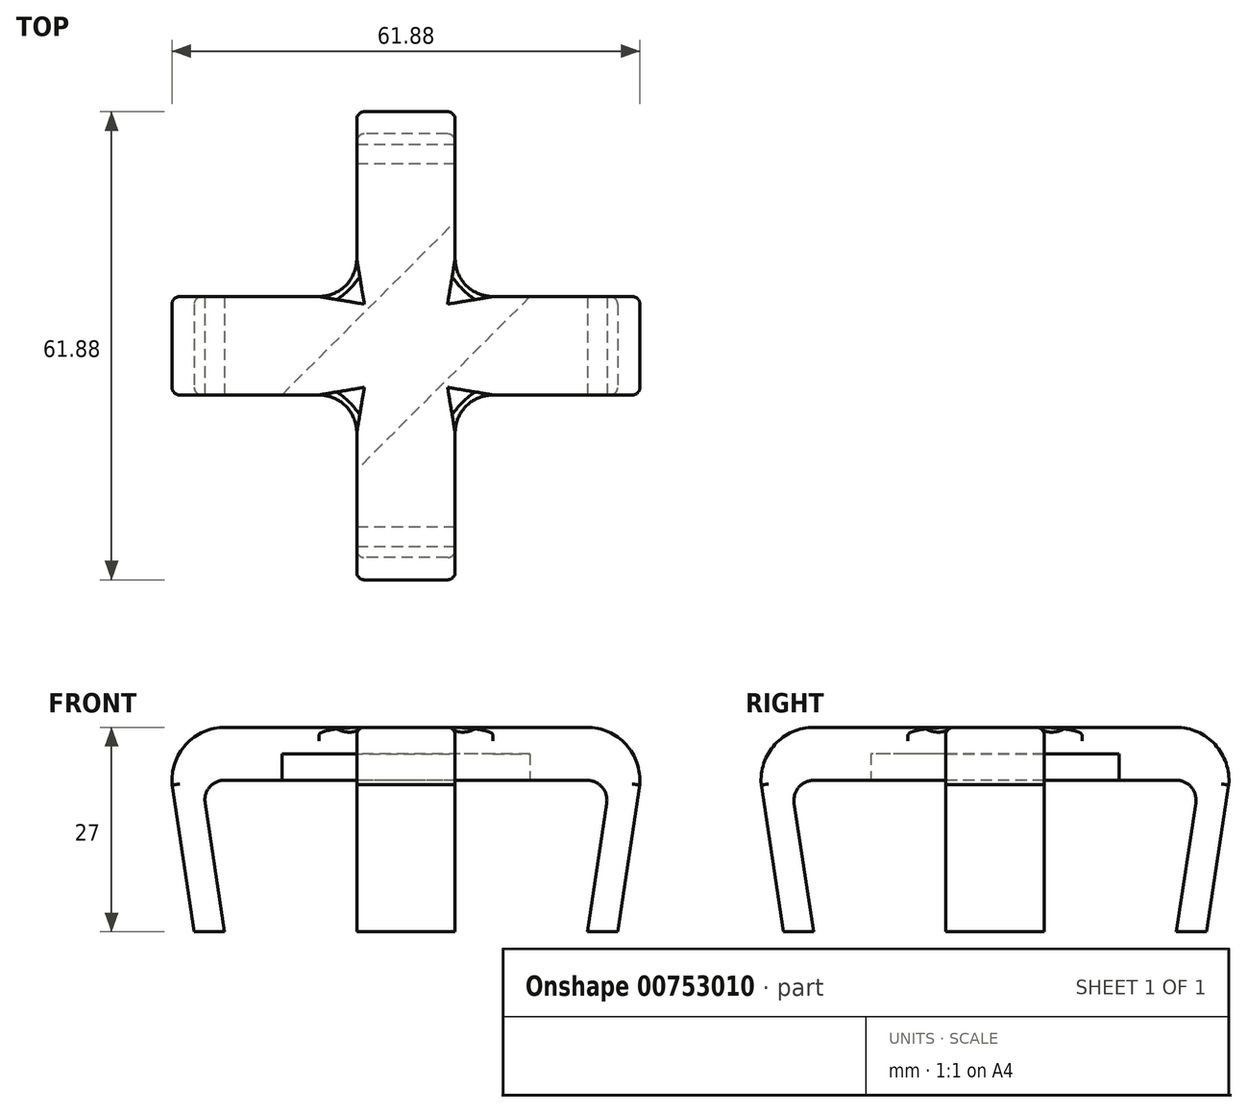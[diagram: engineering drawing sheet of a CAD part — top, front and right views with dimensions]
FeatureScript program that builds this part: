
annotation { "Feature Type Name" : "Feature", "Feature Type Description" : "" }
export const myFeature = defineFeature(function(context is Context, id is Id, definition is map)
    precondition{}
    {
        {
            var Q0;
            Q0=qCreatedBy(makeId("Top.planeOp"),FACE);
            var sketch = newSketch(context, id + "F0", { "sketchPlane" : qUnion([Q0])});
            skLineSegment(sketch, "E0", {"start": v(0, 0) * mm, "end": v(24, 0) * mm});
            skLineSegment(sketch, "E1", {"start": v(0, 0) * mm, "end": v(-24, 0) * mm});
            skLineSegment(sketch, "E2", {"start": v(-24, 20) * mm, "end": v(-28, 20) * mm});
            skLineSegment(sketch, "E3", {"start": v(28, 20) * mm, "end": v(24, 20) * mm});
            skLineSegment(sketch, "E4", {"start": v(-24, 20) * mm, "end": v(-24, 0) * mm, "construction": true});
            skLineSegment(sketch, "E5", {"start": v(-24, 0) * mm, "end": v(-27, 0) * mm, "construction": true});
            skLineSegment(sketch, "E6", {"start": v(24, 0) * mm, "end": v(27, 0) * mm, "construction": true});
            skLineSegment(sketch, "E7", {"start": v(28, 20) * mm, "end": v(30.91, 0.59) * mm});
            skLineSegment(sketch, "E8", {"start": v(30.91, 0.59) * mm, "end": v(27, 0) * mm, "construction": true});
            skLineSegment(sketch, "E9", {"start": v(-28, 20) * mm, "end": v(-30.91, 0.59) * mm});
            skLineSegment(sketch, "E10", {"start": v(-30.91, 0.59) * mm, "end": v(-27, 0) * mm, "construction": true});
            skLineSegment(sketch, "E11", {"start": v(0, 0) * mm, "end": v(0, -7) * mm, "construction": true});
            skLineSegment(sketch, "E12", {"start": v(23.94, -7) * mm, "end": v(-23.94, -7) * mm});
            skArc(sketch, "E13", {"start": v(23.94, -7) * mm, "mid": v(29.09, -4.74) * mm, "end": v(30.91, 0.59) * mm});
            skArc(sketch, "E14", {"start": v(-23.94, -7) * mm, "mid": v(-29.09, -4.74) * mm, "end": v(-30.91, 0.59) * mm});
            skArc(sketch, "E15", {"start": v(-24, 0) * mm, "mid": v(-25.96, 0.9) * mm, "end": v(-26.55, 2.97) * mm});
            skLineSegment(sketch, "E16", {"start": v(24, 20) * mm, "end": v(23.94, 0) * mm, "construction": true});
            skArc(sketch, "E17", {"start": v(24, 0) * mm, "mid": v(25.96, 0.93) * mm, "end": v(26.55, 3.02) * mm});
            skLineSegment(sketch, "E18", {"start": v(24, 20) * mm, "end": v(26.55, 3.02) * mm});
            skLineSegment(sketch, "E19", {"start": v(26.55, 3.02) * mm, "end": v(27, 0) * mm, "construction": true});
            skLineSegment(sketch, "E20", {"start": v(-24, 20) * mm, "end": v(-26.55, 2.97) * mm});
            skLineSegment(sketch, "E21", {"start": v(-26.55, 2.97) * mm, "end": v(-27, 0) * mm, "construction": true});
            skSolve(sketch);
        }
        {
            var Q0;
            Q0=makeQuery(id+"F0.imprint","IMPRINT",FACE,{"disambiguationData":[TD([[makeQuery(id+"F0.imprint","IMPRINT",EDGE,{"derivedFrom":sQuery(id+"F0.wireOp",EDGE,"E0")}),-1.0]])]});
            extrude(context, id + "F1", {"entities" : qUnion([Q0]), "depth" : 13 * mm, "offsetDistance" : 25 * mm});
        }
        {
            var Q0;
            Q0=makeQuery(id+"F1.opExtrude","SWEPT_BODY",BODY,{"disambiguationData":[OSD([sQuery(id+"F0.wireOp",EDGE,"E0"),sQuery(id+"F0.wireOp",EDGE,"E1"),sQuery(id+"F0.wireOp",EDGE,"GqOIY193-nnTG-WNAK-7P5C-qbdsJhsmqnTg"),sQuery(id+"F0.wireOp",EDGE,"nFv10fVA-e4Zq-mQEx-yQo5-pWFaT3uSzO8I"),sQuery(id+"F0.wireOp",EDGE,"E2"),sQuery(id+"F0.wireOp",EDGE,"2eDGChY6-uomO-ZvTw-BVGf-heDjoFAaIxCZ"),sQuery(id+"F0.wireOp",EDGE,"AwENzGN6-6Jdi-Xnei-QJyw-jy8g0ptfrepB"),sQuery(id+"F0.wireOp",EDGE,"pxZ1h7P2-Ql5e-nRXq-oBCs-k8CSoZiUGTe5"),sQuery(id+"F0.wireOp",EDGE,"jQoMa6uT-SFcK-1EqK-lPNF-uQxbUQPNmj6G"),sQuery(id+"F0.wireOp",EDGE,"E3"),sQuery(id+"F0.wireOp",EDGE,"ouRIi9zz-WExV-jkmE-XCtQ-bmmSq9bP91mH"),sQuery(id+"F0.wireOp",EDGE,"O0WKsKBU-VN61-qjR9-eNNd-4MIzQNMGMWZd"),sQuery(id+"F0.wireOp",EDGE,"a8fOSSVA-k9Fx-iGqo-vGb5-aITEA6sK3hfp")])]});
            var Q1;
            {var subQ0=sQuery(id+"F0.wireOp",EDGE,"nFv10fVA-e4Zq-mQEx-yQo5-pWFaT3uSzO8I");var subQ1=sQuery(id+"F0.wireOp",EDGE,"GqOIY193-nnTG-WNAK-7P5C-qbdsJhsmqnTg");var subQ2=sQuery(id+"F0.wireOp",EDGE,"O0WKsKBU-VN61-qjR9-eNNd-4MIzQNMGMWZd");var subQ3=sQuery(id+"F0.wireOp",EDGE,"E1");var subQ4=sQuery(id+"F0.wireOp",EDGE,"E0");Q1=makeQuery(id+"F5.boolean.opBoolean","SPLIT",EDGE,{"disambiguationData":[TD([makeQuery(id+"F4.opFillet","BLEND_FACE",FACE,{"disambiguationData":[OSD([subQ1,subQ0])]})])],"derivedFrom":makeQuery(id+"F1.opExtrude","CAP_EDGE",EDGE,{"disambiguationData":[OSD([subQ4,subQ3,subQ1,subQ2])],"isStart":true})});}
            transform(context, id + "F2", {"entities" : qUnion([Q0]), "transformType" : TransformType.ROTATION, "transformAxis" : qUnion([Q1]), "angle" : 90 * degree, "oppositeDirection" : true, "makeCopy" : false});
        }
        {
            var Q0;
            Q0=qCreatedBy(makeId("Right.planeOp"),FACE);
            var sketch = newSketch(context, id + "F3", { "sketchPlane" : qUnion([Q0])});
            skLineSegment(sketch, "E22.bottom", {"start": v(13, 0) * mm, "end": v(0, 0) * mm, "construction": true});
            skLineSegment(sketch, "E22.top", {"start": v(13, 7) * mm, "end": v(0, 7) * mm, "construction": true});
            skLineSegment(sketch, "E22.left", {"start": v(0, 7) * mm, "end": v(0, 0) * mm, "construction": true});
            skLineSegment(sketch, "E22.right", {"start": v(13, 7) * mm, "end": v(13, 0) * mm, "construction": true});
            skLineSegment(sketch, "E23", {"start": v(6.5, 7) * mm, "end": v(6.5, 0) * mm, "construction": true});
            skSolve(sketch);
        }
        {
            var Q0;
            Q0=makeQuery(id+"F1.opExtrude","CAP_EDGE",EDGE,{"disambiguationData":[OSD([sQuery(id+"F0.wireOp",EDGE,"E12")])],"isStart":true});
            var Q1;
            Q1=makeQuery(id+"F1.opExtrude","CAP_EDGE",EDGE,{"disambiguationData":[OSD([sQuery(id+"F0.wireOp",EDGE,"E12")])],"isStart":false});
            fillet(context, id + "F4", {"entities" : qUnion([Q0, Q1]), "radius" : 1 * mm, "tangentPropagation" : true, "allowEdgeOverflow" : false});
        }
        {
            var Q0;
            Q0=makeQuery(id+"F1.opExtrude","SWEPT_BODY",BODY,{"disambiguationData":[OSD([sQuery(id+"F0.wireOp",EDGE,"E0"),sQuery(id+"F0.wireOp",EDGE,"E1"),sQuery(id+"F0.wireOp",EDGE,"GqOIY193-nnTG-WNAK-7P5C-qbdsJhsmqnTg"),sQuery(id+"F0.wireOp",EDGE,"nFv10fVA-e4Zq-mQEx-yQo5-pWFaT3uSzO8I"),sQuery(id+"F0.wireOp",EDGE,"E2"),sQuery(id+"F0.wireOp",EDGE,"2eDGChY6-uomO-ZvTw-BVGf-heDjoFAaIxCZ"),sQuery(id+"F0.wireOp",EDGE,"AwENzGN6-6Jdi-Xnei-QJyw-jy8g0ptfrepB"),sQuery(id+"F0.wireOp",EDGE,"pxZ1h7P2-Ql5e-nRXq-oBCs-k8CSoZiUGTe5"),sQuery(id+"F0.wireOp",EDGE,"jQoMa6uT-SFcK-1EqK-lPNF-uQxbUQPNmj6G"),sQuery(id+"F0.wireOp",EDGE,"E3"),sQuery(id+"F0.wireOp",EDGE,"ouRIi9zz-WExV-jkmE-XCtQ-bmmSq9bP91mH"),sQuery(id+"F0.wireOp",EDGE,"O0WKsKBU-VN61-qjR9-eNNd-4MIzQNMGMWZd"),sQuery(id+"F0.wireOp",EDGE,"a8fOSSVA-k9Fx-iGqo-vGb5-aITEA6sK3hfp")])]});
            var Q1;
            Q1=sQuery(id+"F3.wireOp",EDGE,"E23");
            circularPattern(context, id + "F5", {"operationType" : NewBodyOperationType.ADD, "entities" : qUnion([Q0]), "axis" : qUnion([Q1]), "angle" : 90 * degree, "instanceCount" : 2, "equalSpace" : true});
        }
        {
            var Q0;
            {var subQ0=sQuery(id+"F0.wireOp",EDGE,"1l9M2pBU-ifvH-zQVZ-bDif-jBtgiZ8Usmep");var subQ1=sQuery(id+"F0.wireOp",EDGE,"8IDM5DlA-q5fv-ob1u-kOfA-MMoOAtUZf9vU");var subQ2=sQuery(id+"F0.wireOp",EDGE,"O0WKsKBU-VN61-qjR9-eNNd-4MIzQNMGMWZd");var subQ3=sQuery(id+"F0.wireOp",EDGE,"ouRIi9zz-WExV-jkmE-XCtQ-bmmSq9bP91mH");var subQ4=sQuery(id+"F0.wireOp",EDGE,"E3");var subQ5=sQuery(id+"F0.wireOp",EDGE,"jQoMa6uT-SFcK-1EqK-lPNF-uQxbUQPNmj6G");var subQ6=sQuery(id+"F0.wireOp",EDGE,"pxZ1h7P2-Ql5e-nRXq-oBCs-k8CSoZiUGTe5");var subQ7=sQuery(id+"F0.wireOp",EDGE,"2eDGChY6-uomO-ZvTw-BVGf-heDjoFAaIxCZ");var subQ8=sQuery(id+"F0.wireOp",EDGE,"E2");var subQ9=sQuery(id+"F0.wireOp",EDGE,"nFv10fVA-e4Zq-mQEx-yQo5-pWFaT3uSzO8I");var subQ10=sQuery(id+"F0.wireOp",EDGE,"GqOIY193-nnTG-WNAK-7P5C-qbdsJhsmqnTg");var subQ11=sQuery(id+"F0.wireOp",EDGE,"E1");var subQ12=sQuery(id+"F0.wireOp",EDGE,"E0");Q0=makeQuery(id+"F5.boolean.opBoolean","INTERSECT",EDGE,{"derivedFrom":[makeQuery(id+"F1.opExtrude","CAP_FACE",FACE,{"disambiguationData":[OSD([subQ12,subQ11,subQ10,subQ9,subQ8,subQ7,subQ6,subQ5,subQ4,subQ3,subQ2,subQ1,subQ0])],"isStart":false}),makeQuery(id+"F5.opPattern","COPY",FACE,{"derivedFrom":makeQuery(id+"F1.opExtrude","CAP_FACE",FACE,{"disambiguationData":[OSD([subQ12,subQ11,subQ10,subQ9,subQ8,subQ7,subQ6,subQ5,subQ4,subQ3,subQ2,subQ1,subQ0])],"isStart":true}),"instanceName":"1"})]});}
            var Q1;
            {var subQ0=sQuery(id+"F0.wireOp",EDGE,"1l9M2pBU-ifvH-zQVZ-bDif-jBtgiZ8Usmep");var subQ1=sQuery(id+"F0.wireOp",EDGE,"8IDM5DlA-q5fv-ob1u-kOfA-MMoOAtUZf9vU");var subQ2=sQuery(id+"F0.wireOp",EDGE,"O0WKsKBU-VN61-qjR9-eNNd-4MIzQNMGMWZd");var subQ3=sQuery(id+"F0.wireOp",EDGE,"ouRIi9zz-WExV-jkmE-XCtQ-bmmSq9bP91mH");var subQ4=sQuery(id+"F0.wireOp",EDGE,"E3");var subQ5=sQuery(id+"F0.wireOp",EDGE,"jQoMa6uT-SFcK-1EqK-lPNF-uQxbUQPNmj6G");var subQ6=sQuery(id+"F0.wireOp",EDGE,"pxZ1h7P2-Ql5e-nRXq-oBCs-k8CSoZiUGTe5");var subQ7=sQuery(id+"F0.wireOp",EDGE,"2eDGChY6-uomO-ZvTw-BVGf-heDjoFAaIxCZ");var subQ8=sQuery(id+"F0.wireOp",EDGE,"E2");var subQ9=sQuery(id+"F0.wireOp",EDGE,"nFv10fVA-e4Zq-mQEx-yQo5-pWFaT3uSzO8I");var subQ10=sQuery(id+"F0.wireOp",EDGE,"GqOIY193-nnTG-WNAK-7P5C-qbdsJhsmqnTg");var subQ11=sQuery(id+"F0.wireOp",EDGE,"E1");var subQ12=sQuery(id+"F0.wireOp",EDGE,"E0");Q1=makeQuery(id+"F5.boolean.opBoolean","INTERSECT",EDGE,{"derivedFrom":[makeQuery(id+"F1.opExtrude","CAP_FACE",FACE,{"disambiguationData":[OSD([subQ12,subQ11,subQ10,subQ9,subQ8,subQ7,subQ6,subQ5,subQ4,subQ3,subQ2,subQ1,subQ0])],"isStart":true}),makeQuery(id+"F5.opPattern","COPY",FACE,{"derivedFrom":makeQuery(id+"F1.opExtrude","CAP_FACE",FACE,{"disambiguationData":[OSD([subQ12,subQ11,subQ10,subQ9,subQ8,subQ7,subQ6,subQ5,subQ4,subQ3,subQ2,subQ1,subQ0])],"isStart":false}),"instanceName":"1"})]});}
            var Q2;
            {var subQ0=makeQuery(id+"F1.opExtrude","CAP_FACE",FACE,{"disambiguationData":[OSD([sQuery(id+"F0.wireOp",EDGE,"E0"),sQuery(id+"F0.wireOp",EDGE,"E1"),sQuery(id+"F0.wireOp",EDGE,"GqOIY193-nnTG-WNAK-7P5C-qbdsJhsmqnTg"),sQuery(id+"F0.wireOp",EDGE,"nFv10fVA-e4Zq-mQEx-yQo5-pWFaT3uSzO8I"),sQuery(id+"F0.wireOp",EDGE,"E2"),sQuery(id+"F0.wireOp",EDGE,"2eDGChY6-uomO-ZvTw-BVGf-heDjoFAaIxCZ"),sQuery(id+"F0.wireOp",EDGE,"pxZ1h7P2-Ql5e-nRXq-oBCs-k8CSoZiUGTe5"),sQuery(id+"F0.wireOp",EDGE,"jQoMa6uT-SFcK-1EqK-lPNF-uQxbUQPNmj6G"),sQuery(id+"F0.wireOp",EDGE,"E3"),sQuery(id+"F0.wireOp",EDGE,"ouRIi9zz-WExV-jkmE-XCtQ-bmmSq9bP91mH"),sQuery(id+"F0.wireOp",EDGE,"O0WKsKBU-VN61-qjR9-eNNd-4MIzQNMGMWZd"),sQuery(id+"F0.wireOp",EDGE,"8IDM5DlA-q5fv-ob1u-kOfA-MMoOAtUZf9vU"),sQuery(id+"F0.wireOp",EDGE,"1l9M2pBU-ifvH-zQVZ-bDif-jBtgiZ8Usmep")])],"isStart":true});Q2=makeQuery(id+"F5.boolean.opBoolean","INTERSECT",EDGE,{"derivedFrom":[subQ0,makeQuery(id+"F5.opPattern","COPY",FACE,{"derivedFrom":subQ0,"instanceName":"1"})]});}
            var Q3;
            {var subQ0=makeQuery(id+"F1.opExtrude","CAP_FACE",FACE,{"disambiguationData":[OSD([sQuery(id+"F0.wireOp",EDGE,"E0"),sQuery(id+"F0.wireOp",EDGE,"E1"),sQuery(id+"F0.wireOp",EDGE,"GqOIY193-nnTG-WNAK-7P5C-qbdsJhsmqnTg"),sQuery(id+"F0.wireOp",EDGE,"nFv10fVA-e4Zq-mQEx-yQo5-pWFaT3uSzO8I"),sQuery(id+"F0.wireOp",EDGE,"E2"),sQuery(id+"F0.wireOp",EDGE,"2eDGChY6-uomO-ZvTw-BVGf-heDjoFAaIxCZ"),sQuery(id+"F0.wireOp",EDGE,"pxZ1h7P2-Ql5e-nRXq-oBCs-k8CSoZiUGTe5"),sQuery(id+"F0.wireOp",EDGE,"jQoMa6uT-SFcK-1EqK-lPNF-uQxbUQPNmj6G"),sQuery(id+"F0.wireOp",EDGE,"E3"),sQuery(id+"F0.wireOp",EDGE,"ouRIi9zz-WExV-jkmE-XCtQ-bmmSq9bP91mH"),sQuery(id+"F0.wireOp",EDGE,"O0WKsKBU-VN61-qjR9-eNNd-4MIzQNMGMWZd"),sQuery(id+"F0.wireOp",EDGE,"8IDM5DlA-q5fv-ob1u-kOfA-MMoOAtUZf9vU"),sQuery(id+"F0.wireOp",EDGE,"1l9M2pBU-ifvH-zQVZ-bDif-jBtgiZ8Usmep")])],"isStart":false});Q3=makeQuery(id+"F5.boolean.opBoolean","INTERSECT",EDGE,{"derivedFrom":[subQ0,makeQuery(id+"F5.opPattern","COPY",FACE,{"derivedFrom":subQ0,"instanceName":"1"})]});}
            fillet(context, id + "F6", {"entities" : qUnion([Q0, Q1, Q2, Q3]), "radius" : 5 * mm, "tangentPropagation" : true, "allowEdgeOverflow" : false});
        }
        {
            var Q0;
            {var subQ0=makeQuery(id+"F1.opExtrude","SWEPT_FACE",FACE,{"disambiguationData":[OSD([sQuery(id+"F0.wireOp",EDGE,"E0"),sQuery(id+"F0.wireOp",EDGE,"E1"),sQuery(id+"F0.wireOp",EDGE,"GqOIY193-nnTG-WNAK-7P5C-qbdsJhsmqnTg"),sQuery(id+"F0.wireOp",EDGE,"O0WKsKBU-VN61-qjR9-eNNd-4MIzQNMGMWZd")])]});Q0=makeQuery(id+"F5.boolean.opBoolean","MERGE",FACE,{"derivedFrom":[subQ0,makeQuery(id+"F5.opPattern","COPY",FACE,{"derivedFrom":subQ0,"instanceName":"1"})]});}
            var sketch = newSketch(context, id + "F7", { "sketchPlane" : qUnion([Q0])});
            skLineSegment(sketch, "E24", {"start": v(7.96, 1.46) * mm, "end": v(7.96, -14.46) * mm, "construction": true});
            skLineSegment(sketch, "E25", {"start": v(7.96, -14.46) * mm, "end": v(-7.96, -14.46) * mm, "construction": true});
            skLineSegment(sketch, "E26", {"start": v(-7.96, -14.46) * mm, "end": v(-7.96, 1.46) * mm, "construction": true});
            skLineSegment(sketch, "E27", {"start": v(-7.96, 1.46) * mm, "end": v(7.96, 1.46) * mm, "construction": true});
            skLineSegment(sketch, "E28", {"start": v(7.96, -14.46) * mm, "end": v(-7.96, 1.46) * mm, "construction": true});
            skLineSegment(sketch, "E29", {"start": v(7.96, -14.46) * mm, "end": v(23.9, -30.4) * mm, "construction": true});
            skLineSegment(sketch, "E30", {"start": v(-7.96, 1.46) * mm, "end": v(-23.9, 17.4) * mm, "construction": true});
            skLineSegment(sketch, "E31", {"start": v(-23.9, 17.4) * mm, "end": v(-18.94, 22.34) * mm});
            skLineSegment(sketch, "E32", {"start": v(23.9, -30.4) * mm, "end": v(28.84, -25.44) * mm});
            skLineSegment(sketch, "E33", {"start": v(23.9, -30.4) * mm, "end": v(18.94, -35.34) * mm});
            skPoint(sketch, "E34.endSnap0", {"position": v(-15.93, 9.43) * mm});
            skLineSegment(sketch, "E35", {"start": v(28.84, -25.44) * mm, "end": v(-18.94, 22.34) * mm});
            skLineSegment(sketch, "E36", {"start": v(-23.9, 17.4) * mm, "end": v(-28.84, 12.44) * mm});
            skLineSegment(sketch, "E37", {"start": v(-28.84, 12.44) * mm, "end": v(18.94, -35.34) * mm});
            skSolve(sketch);
        }
        {
            var Q0;
            {var subQ0=sQuery(id+"F0.wireOp",EDGE,"E1");var subQ1=sQuery(id+"F0.wireOp",EDGE,"E0");var subQ2=makeQuery(id+"F1.opExtrude","SWEPT_FACE",FACE,{"disambiguationData":[OSD([subQ1,subQ0])]});var subQ3=makeQuery(id+"F5.opPattern","COPY",FACE,{"derivedFrom":subQ2,"instanceName":"1"});var subQ4=makeQuery(id+"F5.boolean.opBoolean","MERGE",FACE,{"derivedFrom":[subQ2,subQ3]});var subQ5=sQuery(id+"F0.wireOp",EDGE,"E20");var subQ6=sQuery(id+"F0.wireOp",EDGE,"E18");var subQ7=sQuery(id+"F0.wireOp",EDGE,"E17");var subQ8=sQuery(id+"F0.wireOp",EDGE,"E15");var subQ9=sQuery(id+"F0.wireOp",EDGE,"E14");var subQ10=sQuery(id+"F0.wireOp",EDGE,"E13");var subQ11=sQuery(id+"F0.wireOp",EDGE,"E12");var subQ12=sQuery(id+"F0.wireOp",EDGE,"E9");var subQ13=sQuery(id+"F0.wireOp",EDGE,"E7");var subQ14=sQuery(id+"F0.wireOp",EDGE,"E3");var subQ15=sQuery(id+"F0.wireOp",EDGE,"E2");var subQ16=makeQuery(id+"F1.opExtrude","CAP_FACE",FACE,{"disambiguationData":[OSD([subQ1,subQ0,subQ15,subQ14,subQ13,subQ12,subQ11,subQ10,subQ9,subQ8,subQ7,subQ6,subQ5])],"isStart":true});var subQ17=subQ16;var subQ18=makeQuery(id+"F5.opPattern","COPY",FACE,{"derivedFrom":subQ17,"instanceName":"1"});var subQ19=makeQuery(id+"F6.opFillet","BLEND_EDGE",EDGE,{"blendedFrom":[makeQuery(id+"F5.boolean.opBoolean","INTERSECT",EDGE,{"derivedFrom":[subQ17,subQ18]}),subQ4],"blendedInto":[subQ4]});Q0=makeQuery(id+"F7.imprint","IMPRINT",FACE,{"disambiguationData":[TD([[makeQuery(id+"F7.imprint","IMPRINT",EDGE,{"derivedFrom":subQ19}),1.0]])]});}
            extrude(context, id + "F8", {"entities" : qUnion([Q0]), "operationType" : NewBodyOperationType.REMOVE, "oppositeDirection" : true, "depth" : 3.5 * mm, "offsetDistance" : 25 * mm});
        }
    });
